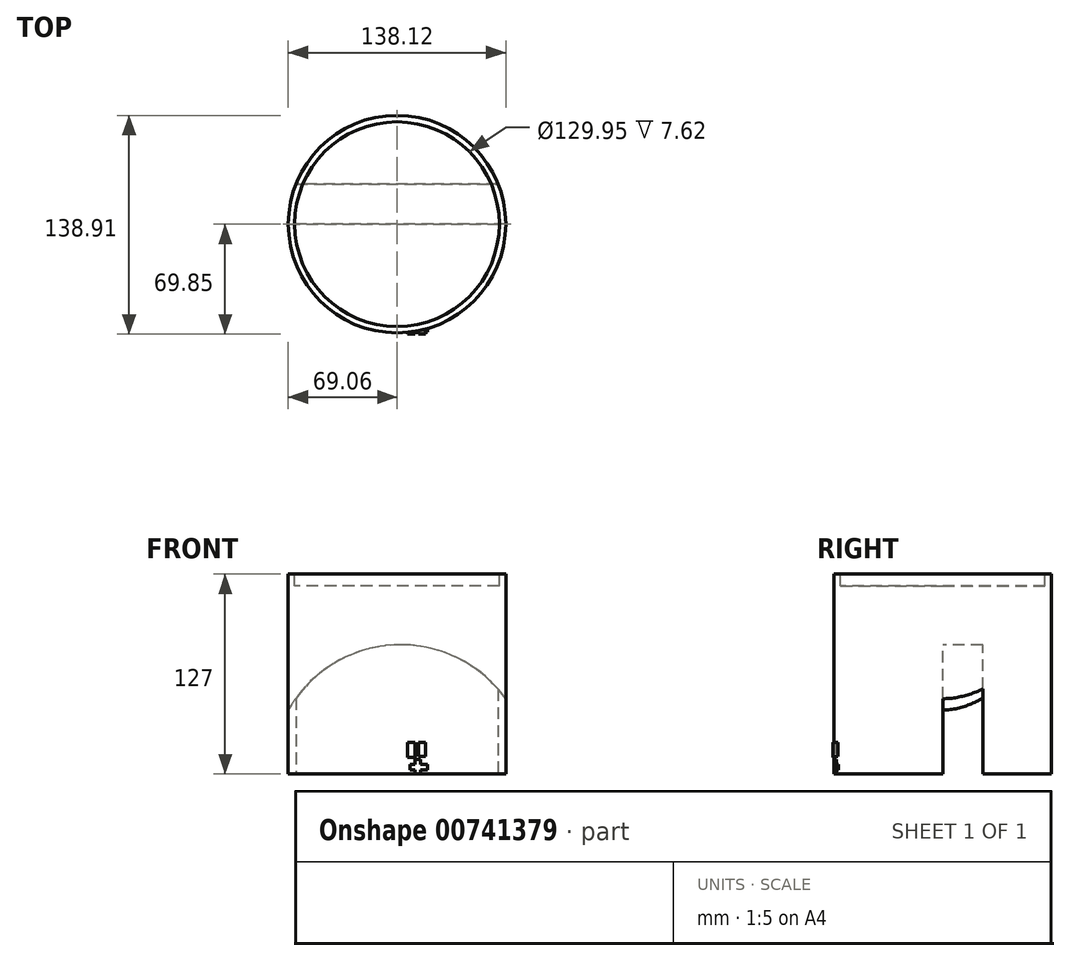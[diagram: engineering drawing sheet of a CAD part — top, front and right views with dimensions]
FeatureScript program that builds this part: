
annotation { "Feature Type Name" : "Feature", "Feature Type Description" : "" }
export const myFeature = defineFeature(function(context is Context, id is Id, definition is map)
    precondition{}
    {
        {
            var Q0;
            Q0=qCreatedBy(makeId("Top.planeOp"),FACE);
            var sketch = newSketch(context, id + "F0", { "sketchPlane" : qUnion([Q0])});
            skCircle(sketch, "E0", {"center": v(0, 0) * mm, "radius": 69.06 * mm});
            skSolve(sketch);
        }
        {
            var Q0;
            Q0 = qSketchRegion(id + "F0", true);
            extrude(context, id + "F1", {"entities" : qUnion([Q0]), "depth" : 127 * mm, "offsetDistance" : 25.4 * mm});
        }
        {
            var Q0;
            Q0=qCreatedBy(makeId("Front.planeOp"),FACE);
            var sketch = newSketch(context, id + "F2", { "sketchPlane" : qUnion([Q0])});
            skCircle(sketch, "E1", {"center": v(2.31, 0) * mm, "radius": 82.15 * mm});
            skSolve(sketch);
        }
        {
            var Q0;
            Q0 = qSketchRegion(id + "F2", true);
            extrude(context, id + "F3", {"entities" : qUnion([Q0]), "operationType" : NewBodyOperationType.REMOVE, "oppositeDirection" : true, "depth" : 25.4 * mm, "offsetDistance" : 25.4 * mm});
        }
        {
            var Q0;
            Q0=makeQuery(id+"F1.opExtrude","CAP_FACE",FACE,{"disambiguationData":[OSD([sQuery(id+"F0.wireOp",EDGE,"E0")])],"isStart":false});
            var sketch = newSketch(context, id + "F4", { "sketchPlane" : qUnion([Q0])});
            skCircle(sketch, "E2", {"center": v(0, 0) * mm, "radius": 64.98 * mm});
            skSolve(sketch);
        }
        {
            var Q0;
            Q0 = qSketchRegion(id + "F4", true);
            extrude(context, id + "F5", {"entities" : qUnion([Q0]), "operationType" : NewBodyOperationType.REMOVE, "oppositeDirection" : true, "depth" : 7.62 * mm, "offsetDistance" : 25.4 * mm});
        }
        {
            var Q0;
            Q0=qCreatedBy(makeId("Front.planeOp"),FACE);
            var sketch = newSketch(context, id + "F6", { "sketchPlane" : qUnion([Q0])});
            skLineSegment(sketch, "E3.bottom", {"start": v(11.34, 0) * mm, "end": v(15.02, 0) * mm});
            skLineSegment(sketch, "E3.top", {"start": v(11.34, 9.28) * mm, "end": v(15.02, 9.28) * mm});
            skLineSegment(sketch, "E3.left", {"start": v(11.34, 0) * mm, "end": v(11.34, 9.28) * mm});
            skLineSegment(sketch, "E3.right", {"start": v(15.02, 0) * mm, "end": v(15.02, 9.28) * mm});
            skSolve(sketch);
        }
        {
            var Q0;
            Q0 = qSketchRegion(id + "F6", true);
            extrude(context, id + "F7", {"entities" : qUnion([Q0]), "operationType" : NewBodyOperationType.ADD, "depth" : 68.58 * mm, "offsetDistance" : 25.4 * mm});
        }
        {
            var Q0;
            Q0=qCreatedBy(makeId("Front.planeOp"),FACE);
            var sketch = newSketch(context, id + "F8", { "sketchPlane" : qUnion([Q0])});
            skLineSegment(sketch, "E4.bottom", {"start": v(7.79, 6.13) * mm, "end": v(19.42, 6.13) * mm});
            skLineSegment(sketch, "E4.top", {"start": v(7.79, 2.6) * mm, "end": v(19.42, 2.6) * mm});
            skLineSegment(sketch, "E4.left", {"start": v(7.79, 6.13) * mm, "end": v(7.79, 2.6) * mm});
            skLineSegment(sketch, "E4.right", {"start": v(19.42, 6.13) * mm, "end": v(19.42, 2.6) * mm});
            skSolve(sketch);
        }
        {
            var Q0;
            Q0 = qSketchRegion(id + "F8", true);
            extrude(context, id + "F9", {"entities" : qUnion([Q0]), "operationType" : NewBodyOperationType.ADD, "depth" : 68.58 * mm, "offsetDistance" : 25.4 * mm});
        }
        {
            var Q0;
            Q0=qCreatedBy(makeId("Front.planeOp"),FACE);
            var sketch = newSketch(context, id + "F10", { "sketchPlane" : qUnion([Q0])});
            skLineSegment(sketch, "E5.bottom", {"start": v(6.54, 20.25) * mm, "end": v(11.32, 20.25) * mm});
            skLineSegment(sketch, "E5.top", {"start": v(6.54, 10.49) * mm, "end": v(11.32, 10.49) * mm});
            skLineSegment(sketch, "E5.left", {"start": v(6.54, 20.25) * mm, "end": v(6.54, 10.49) * mm});
            skLineSegment(sketch, "E5.right", {"start": v(11.32, 20.25) * mm, "end": v(11.32, 10.49) * mm});
            skSolve(sketch);
        }
        {
            var Q0;
            Q0 = qSketchRegion(id + "F10", true);
            extrude(context, id + "F11", {"entities" : qUnion([Q0]), "operationType" : NewBodyOperationType.ADD, "depth" : 69.85 * mm, "offsetDistance" : 25.4 * mm});
        }
        {
            var Q0;
            Q0=qCreatedBy(makeId("Front.planeOp"),FACE);
            var sketch = newSketch(context, id + "F12", { "sketchPlane" : qUnion([Q0])});
            skLineSegment(sketch, "E6.bottom", {"start": v(13.6, 11.11) * mm, "end": v(18.17, 11.11) * mm});
            skLineSegment(sketch, "E6.top", {"start": v(13.6, 20.25) * mm, "end": v(18.17, 20.25) * mm});
            skLineSegment(sketch, "E6.left", {"start": v(13.6, 11.11) * mm, "end": v(13.6, 20.25) * mm});
            skLineSegment(sketch, "E6.right", {"start": v(18.17, 11.11) * mm, "end": v(18.17, 20.25) * mm});
            skSolve(sketch);
        }
        {
            var Q0;
            Q0 = qSketchRegion(id + "F12", true);
            extrude(context, id + "F13", {"entities" : qUnion([Q0]), "operationType" : NewBodyOperationType.ADD, "depth" : 69.85 * mm, "offsetDistance" : 25.4 * mm});
        }
    });
